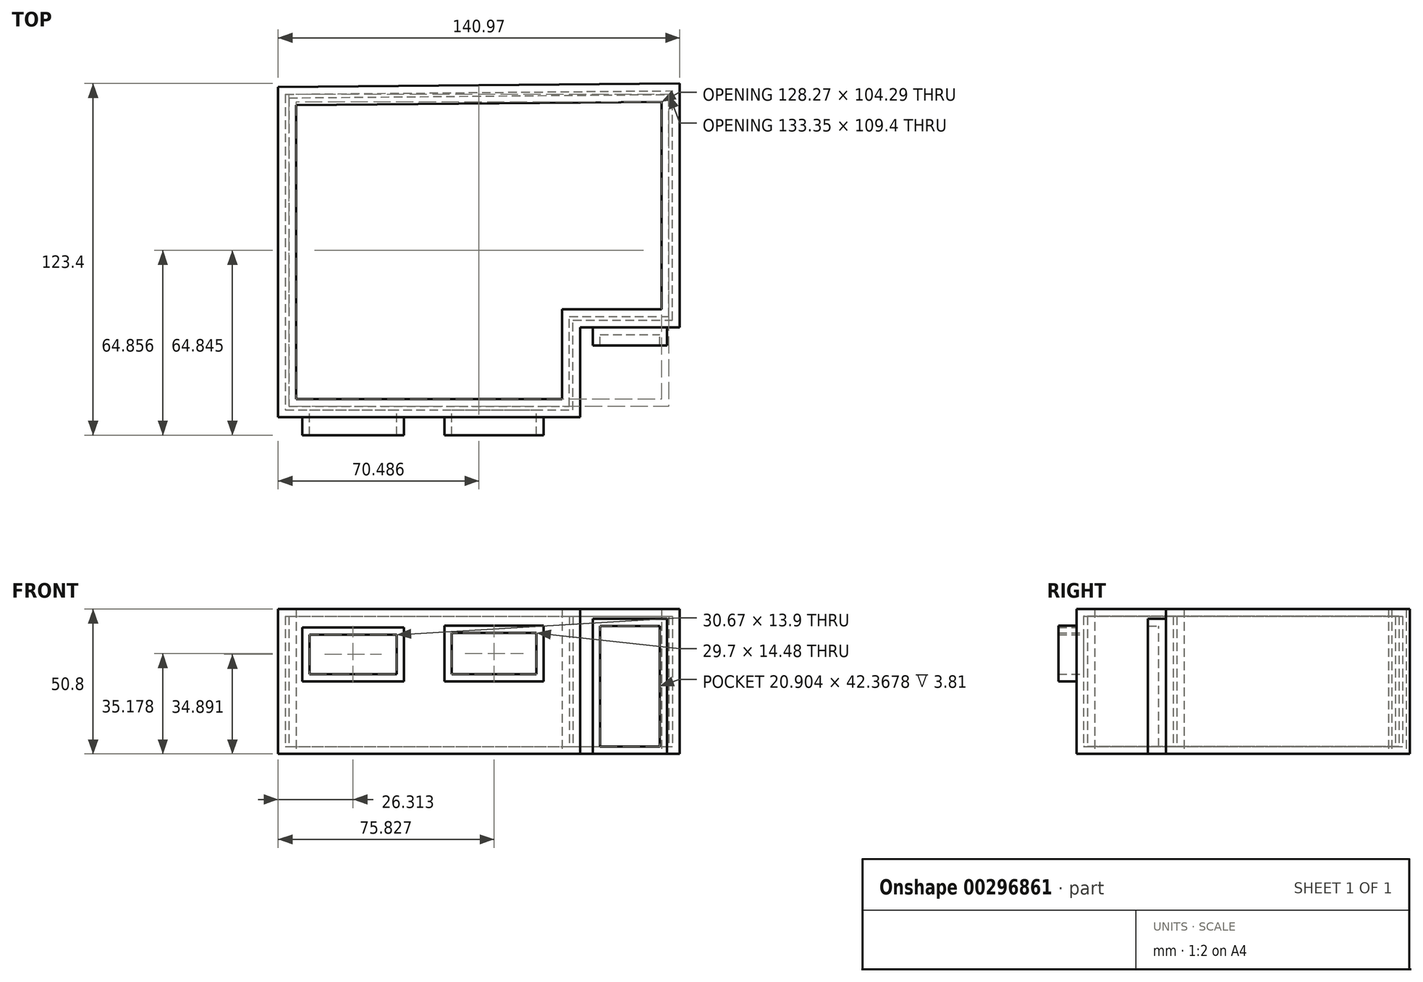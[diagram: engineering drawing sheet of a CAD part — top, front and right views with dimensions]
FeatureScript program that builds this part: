
annotation { "Feature Type Name" : "Feature", "Feature Type Description" : "" }
export const myFeature = defineFeature(function(context is Context, id is Id, definition is map)
    precondition{}
    {
        {
            var Q0;
            Q0=qCreatedBy(makeId("Top.planeOp"),FACE);
            var sketch = newSketch(context, id + "F0", { "sketchPlane" : qUnion([Q0])});
            skLineSegment(sketch, "E0", {"start": v(-57.78, 53.74) * mm, "end": v(-57.78, -49.4) * mm});
            skLineSegment(sketch, "E1", {"start": v(-57.78, -49.4) * mm, "end": v(35.53, -49.4) * mm});
            skLineSegment(sketch, "E2", {"start": v(35.53, -49.4) * mm, "end": v(35.53, -17.91) * mm});
            skLineSegment(sketch, "E3", {"start": v(35.53, -17.91) * mm, "end": v(70.5, -17.91) * mm});
            skLineSegment(sketch, "E4", {"start": v(70.5, -17.91) * mm, "end": v(70.5, 54.9) * mm});
            skLineSegment(sketch, "E5", {"start": v(-57.78, 53.74) * mm, "end": v(70.5, 54.9) * mm});
            skLineSegment(sketch, "E6.0", {"start": v(-64.13, 60.03) * mm, "end": v(76.84, 61.3) * mm});
            skLineSegment(sketch, "E6.1", {"start": v(-64.13, -55.75) * mm, "end": v(41.88, -55.75) * mm});
            skLineSegment(sketch, "E6.2", {"start": v(41.88, -55.75) * mm, "end": v(41.88, -24.26) * mm});
            skLineSegment(sketch, "E6.3", {"start": v(-64.13, 60.03) * mm, "end": v(-64.13, -55.75) * mm});
            skLineSegment(sketch, "E6.4", {"start": v(41.88, -24.26) * mm, "end": v(76.84, -24.26) * mm});
            skLineSegment(sketch, "E6.5", {"start": v(76.84, -24.26) * mm, "end": v(76.84, 61.3) * mm});
            skSolve(sketch);
        }
        {
            var Q0;
            Q0=makeQuery(id+"F0.imprint","IMPRINT",FACE,{"disambiguationData":[TD([[makeQuery(id+"F0.imprint","IMPRINT",EDGE,{"derivedFrom":sQuery(id+"F0.wireOp",EDGE,"E0")}),-1.0]])]});
            var Q1;
            Q1=sQuery(id+"F0.wireOp",EDGE,"E6.1");
            var Q2;
            Q2=sQuery(id+"F0.wireOp",EDGE,"E3");
            var Q3;
            Q3=sQuery(id+"F0.wireOp",EDGE,"E6.2");
            var Q4;
            Q4=sQuery(id+"F0.wireOp",EDGE,"E5");
            var Q5;
            Q5=sQuery(id+"F0.wireOp",EDGE,"E4");
            var Q6;
            Q6=sQuery(id+"F0.wireOp",EDGE,"E6.3");
            var Q7;
            Q7=sQuery(id+"F0.wireOp",EDGE,"E2");
            var Q8;
            Q8=sQuery(id+"F0.wireOp",EDGE,"E6.4");
            var Q9;
            Q9=sQuery(id+"F0.wireOp",EDGE,"E6.5");
            var Q10;
            Q10=sQuery(id+"F0.wireOp",EDGE,"E6.0");
            var Q11;
            Q11=sQuery(id+"F0.wireOp",EDGE,"E0");
            var Q12;
            Q12=sQuery(id+"F0.wireOp",EDGE,"E1");
            extrude(context, id + "F1", {"entities" : qUnion([Q0]), "surfaceEntities" : qUnion([Q1, Q2, Q3, Q4, Q5, Q6, Q7, Q8, Q9, Q10, Q11, Q12]), "endBound" : BoundingType.SYMMETRIC, "depth" : 50.8 * mm});
        }
        {
            var Q0;
            Q0=makeQuery(id+"F1.opExtrude","SWEPT_FACE",FACE,{"disambiguationData":[OSD([sQuery(id+"F0.wireOp",EDGE,"E6.1")])]});
            var sketch = newSketch(context, id + "F2", { "sketchPlane" : qUnion([Q0])});
            skLineSegment(sketch, "E7.bottom", {"start": v(-55.7, 18.98) * mm, "end": v(-19.94, 18.98) * mm});
            skLineSegment(sketch, "E7.top", {"start": v(-55.7, 0) * mm, "end": v(-19.94, 0) * mm});
            skLineSegment(sketch, "E7.left", {"start": v(-55.7, 18.98) * mm, "end": v(-55.7, 0) * mm});
            skLineSegment(sketch, "E7.right", {"start": v(-19.94, 18.98) * mm, "end": v(-19.94, 0) * mm});
            skLineSegment(sketch, "E8.bottom", {"start": v(-5.7, 19.56) * mm, "end": v(29.09, 19.56) * mm});
            skLineSegment(sketch, "E8.top", {"start": v(-5.7, 0) * mm, "end": v(29.09, 0) * mm});
            skLineSegment(sketch, "E8.left", {"start": v(-5.7, 19.56) * mm, "end": v(-5.7, 0) * mm});
            skLineSegment(sketch, "E8.right", {"start": v(29.09, 19.56) * mm, "end": v(29.09, 0) * mm});
            skSolve(sketch);
        }
        {
            var Q0;
            Q0=makeQuery(id+"F2.imprint","IMPRINT",FACE,{"disambiguationData":[TD([[makeQuery(id+"F2.imprint","IMPRINT",EDGE,{"derivedFrom":sQuery(id+"F2.wireOp",EDGE,"E7.bottom")}),-1.0]])]});
            var Q1;
            Q1=makeQuery(id+"F2.imprint","IMPRINT",FACE,{"disambiguationData":[TD([[makeQuery(id+"F2.imprint","IMPRINT",EDGE,{"derivedFrom":sQuery(id+"F2.wireOp",EDGE,"E8.bottom")}),-1.0]])]});
            extrude(context, id + "F3", {"entities" : qUnion([Q0, Q1]), "operationType" : NewBodyOperationType.ADD, "depth" : 6.35 * mm});
        }
        {
            var Q0;
            Q0=makeQuery(id+"F1.opExtrude","SWEPT_FACE",FACE,{"disambiguationData":[OSD([sQuery(id+"F0.wireOp",EDGE,"E6.4")])]});
            var sketch = newSketch(context, id + "F4", { "sketchPlane" : qUnion([Q0])});
            skLineSegment(sketch, "E9.bottom", {"start": v(46.32, -25.4) * mm, "end": v(72.3, -25.4) * mm});
            skLineSegment(sketch, "E9.top", {"start": v(46.32, 22.05) * mm, "end": v(72.3, 22.05) * mm});
            skLineSegment(sketch, "E9.left", {"start": v(46.32, -25.4) * mm, "end": v(46.32, 22.05) * mm});
            skLineSegment(sketch, "E9.right", {"start": v(72.3, -25.4) * mm, "end": v(72.3, 22.05) * mm});
            skSolve(sketch);
        }
        {
            var Q0;
            Q0 = qSketchRegion(id + "F4", true);
            extrude(context, id + "F5", {"entities" : qUnion([Q0]), "depth" : 6.35 * mm});
        }
        {
            var Q0;
            Q0=makeQuery(id+"F3.opExtrude","CAP_FACE",FACE,{"disambiguationData":[OSD([sQuery(id+"F2.wireOp",EDGE,"E7.bottom"),sQuery(id+"F2.wireOp",EDGE,"E7.top"),sQuery(id+"F2.wireOp",EDGE,"E7.left"),sQuery(id+"F2.wireOp",EDGE,"E7.right")])],"isStart":false});
            var Q1;
            Q1=makeQuery(id+"F3.opExtrude","CAP_FACE",FACE,{"disambiguationData":[OSD([sQuery(id+"F2.wireOp",EDGE,"E8.bottom"),sQuery(id+"F2.wireOp",EDGE,"E8.top"),sQuery(id+"F2.wireOp",EDGE,"E8.left"),sQuery(id+"F2.wireOp",EDGE,"E8.right")])],"isStart":false});
            var Q2;
            Q2=makeQuery(id+"F5.opExtrude","CAP_FACE",FACE,{"disambiguationData":[OSD([sQuery(id+"F4.wireOp",EDGE,"E9.bottom"),sQuery(id+"F4.wireOp",EDGE,"E9.top"),sQuery(id+"F4.wireOp",EDGE,"E9.left"),sQuery(id+"F4.wireOp",EDGE,"E9.right")])],"isStart":false});
            shell(context, id + "F6", {"entities" : qUnion([Q0, Q1, Q2]), "thickness" : 2.54 * mm});
        }
    });
